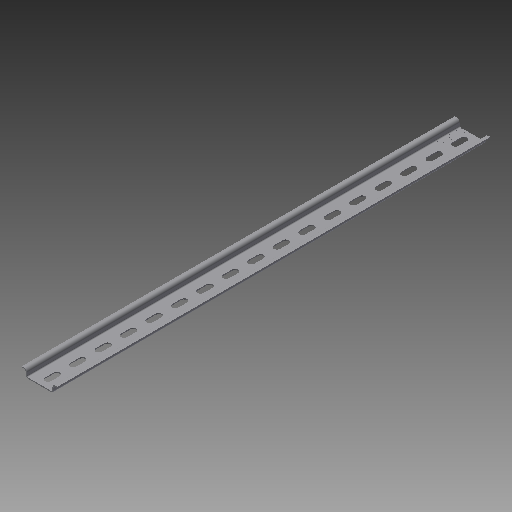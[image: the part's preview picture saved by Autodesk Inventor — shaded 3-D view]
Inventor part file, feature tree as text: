
AUTODESK INVENTOR PART (.ipt)
format: ipt  version: 2017 (Build 210142000, 142)  size: 333,312 bytes
history: native  units: in
note: dims shown in document units (in); Inventor stores cm internally (conversion verified against a paired STEP export)
features: sketch x2, other x1, plane x1, extrude x1, imported_body x1, projected_geometry x1
ambient origin geometry x8: Origin, YZ Plane, XZ Plane, XY Plane, X Axis, Y Axis, Z Axis, Center Point
bodies: Solid1 (feature_tree)
feature tree (7):
  other  "www_techna_eu-DIN 35 Rail-DEFAULT.SAT1"
  plane  "Work Plane1"
  sketch  "Sketch1"  dims[d0=16.7323in d1=0.0in d2=0.0in]
  extrude  "Extrusion1"  TaperAngle=0.0deg  [1 undecoded]
  imported_body  "Base1"
  sketch  "Sketch2"
  projected_geometry  "Projected Loop1"
note: 1 required parameter value undecoded (feature->parameter linkage not recoverable at this tier; creation-order binding heuristic only, values carry confidence <= 0.55)
